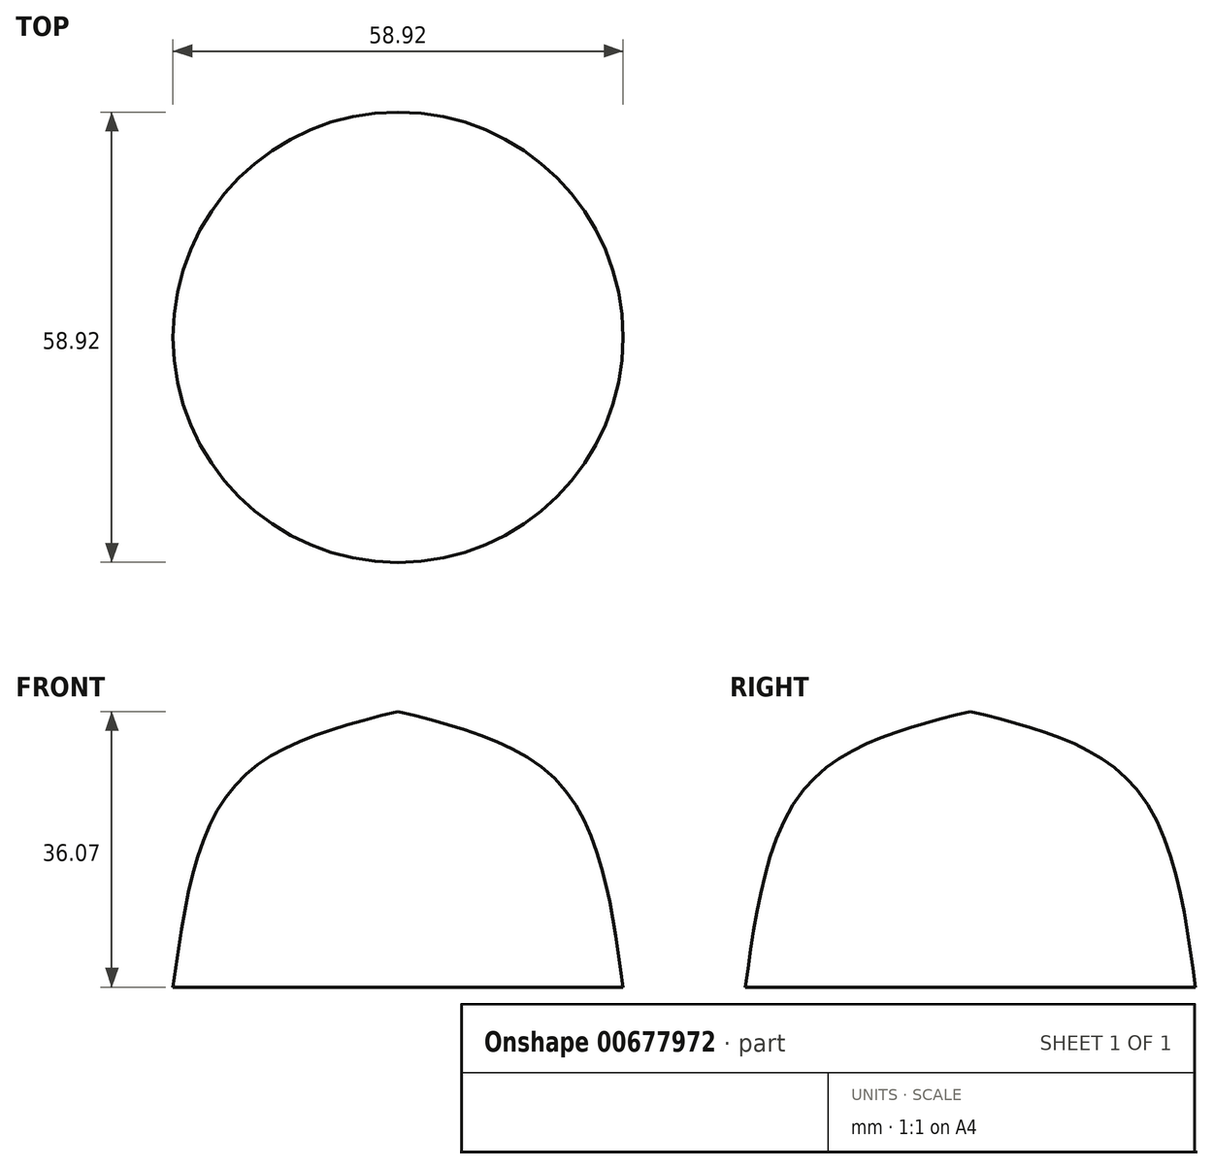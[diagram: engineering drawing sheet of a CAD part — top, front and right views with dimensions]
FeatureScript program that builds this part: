
annotation { "Feature Type Name" : "Feature", "Feature Type Description" : "" }
export const myFeature = defineFeature(function(context is Context, id is Id, definition is map)
    precondition{}
    {
        {
            var Q0;
            Q0=qCreatedBy(makeId("Front.planeOp"),FACE);
            var sketch = newSketch(context, id + "F0", { "sketchPlane" : qUnion([Q0])});
            skLineSegment(sketch, "E0", {"start": v(0, 0) * mm, "end": v(-36.83, 0) * mm});
            skFitSpline(sketch, "E1", {"points": [v(-36.83, 0) * mm, v(-26.72, 32.95) * mm, v(0, 45.09) * mm], "startDerivative": vector(10.02, 73.26) * mm, "endDerivative": vector(64.37, 16.16) * mm});
            skLineSegment(sketch, "E2", {"start": v(0, 45.09) * mm, "end": v(0, 0) * mm});
            skSolve(sketch);
        }
        {
            var Q0;
            Q0=makeQuery(id+"F0.imprint","IMPRINT",FACE,{"disambiguationData":[TD([[makeQuery(id+"F0.imprint","IMPRINT",EDGE,{"derivedFrom":sQuery(id+"F0.wireOp",EDGE,"E0")}),-1.0]])]});
            var Q1;
            Q1=sQuery(id+"F0.wireOp",EDGE,"E2");
            revolve(context, id + "F1", {"entities" : qUnion([Q0]), "axis" : qUnion([Q1]), "revolveType" : RevolveType.FULL});
        }
        {
            var Q0;
            Q0=makeQuery(id+"F1.opRevolve","SWEPT_BODY",BODY,{"disambiguationData":[OSD([sQuery(id+"F0.wireOp",EDGE,"E0"),sQuery(id+"F0.wireOp",EDGE,"E1"),sQuery(id+"F0.wireOp",EDGE,"E2")])]});
            var Q1;
            Q1=qCreatedBy(makeId("Origin.pointOp"),VERTEX);
            transform(context, id + "F2", {"entities" : qUnion([Q0]), "transformType" : TransformType.SCALE_UNIFORMLY, "scale" : .8, "scalePoint" : qUnion([Q1]), "makeCopy" : false});
        }
    });
